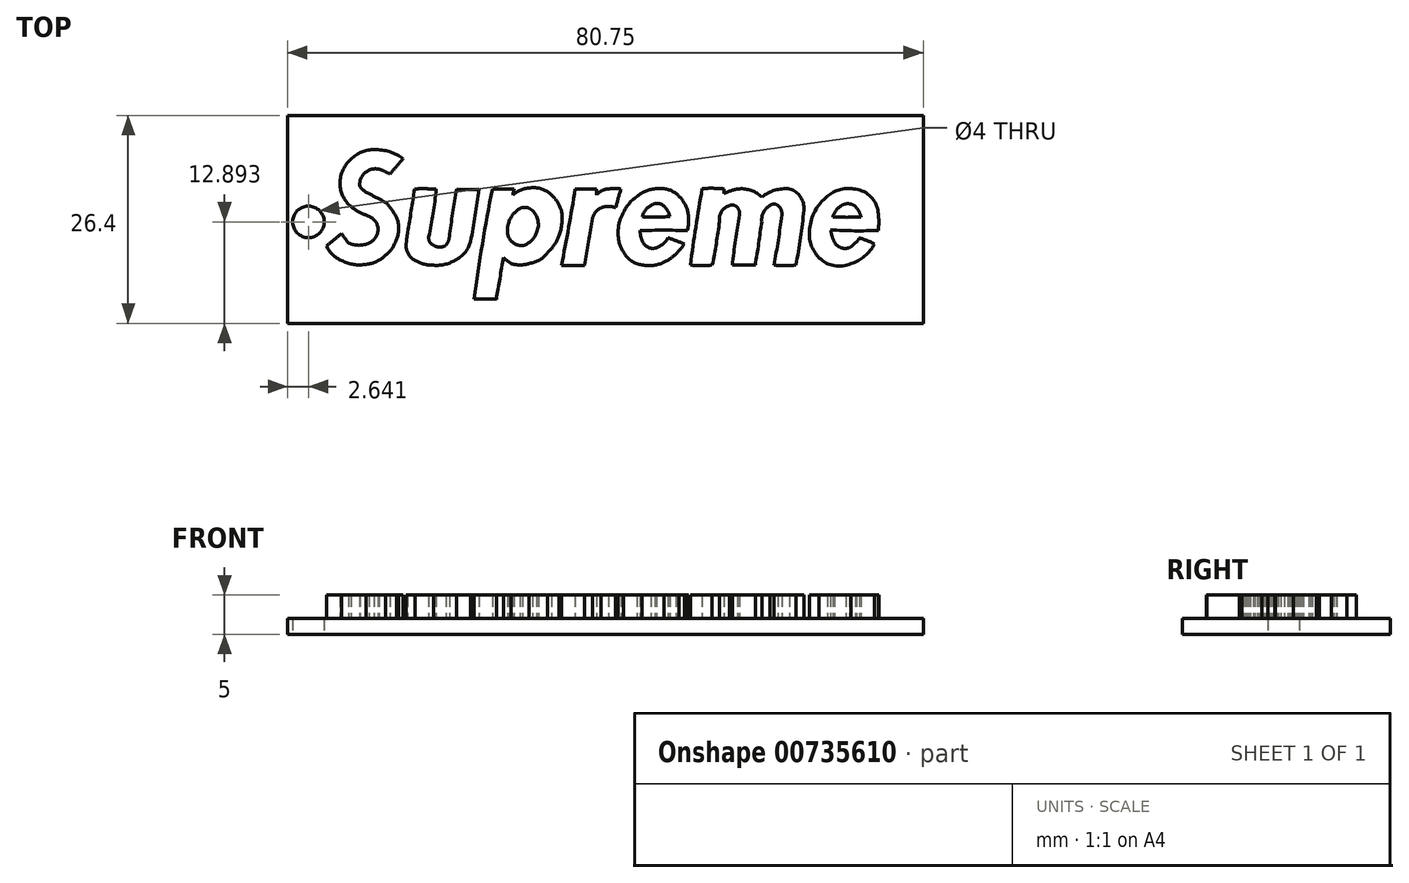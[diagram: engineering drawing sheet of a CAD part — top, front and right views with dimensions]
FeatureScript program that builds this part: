
annotation { "Feature Type Name" : "Feature", "Feature Type Description" : "" }
export const myFeature = defineFeature(function(context is Context, id is Id, definition is map)
    precondition{}
    {
        {
            var Q0;
            Q0=qCreatedBy(makeId("Top.planeOp"),FACE);
            var sketch = newSketch(context, id + "F0", { "sketchPlane" : qUnion([Q0])});
            skArc(sketch, "E0", {"start": v(-34.63, 20.9) * mm, "mid": v(-36.37, 21.8) * mm, "end": v(-38.3, 22.08) * mm});
            skArc(sketch, "E1", {"start": v(-38.3, 22.08) * mm, "mid": v(-39.9, 21.77) * mm, "end": v(-41.25, 20.87) * mm});
            skArc(sketch, "E2", {"start": v(-41.25, 20.87) * mm, "mid": v(-42.35, 19.34) * mm, "end": v(-42.67, 17.5) * mm});
            skArc(sketch, "E3", {"start": v(-42.67, 17.5) * mm, "mid": v(-42.22, 16.03) * mm, "end": v(-41.25, 14.83) * mm});
            skArc(sketch, "E4", {"start": v(-41.25, 14.83) * mm, "mid": v(-40.34, 14.21) * mm, "end": v(-39.34, 13.75) * mm});
            skArc(sketch, "E5", {"start": v(-37.84, 12.2) * mm, "mid": v(-38.36, 13.2) * mm, "end": v(-39.34, 13.75) * mm});
            skArc(sketch, "E6", {"start": v(-38.96, 10.2) * mm, "mid": v(-38.09, 11.03) * mm, "end": v(-37.84, 12.2) * mm});
            skArc(sketch, "E7", {"start": v(-41.55, 10.2) * mm, "mid": v(-40.26, 9.92) * mm, "end": v(-38.96, 10.2) * mm});
            skArc(sketch, "E8", {"start": v(-42.46, 11.41) * mm, "mid": v(-42.03, 10.8) * mm, "end": v(-41.55, 10.2) * mm});
            skArc(sketch, "E9", {"start": v(-44.38, 9.83) * mm, "mid": v(-43.42, 10.62) * mm, "end": v(-42.46, 11.41) * mm});
            skArc(sketch, "E10", {"start": v(-44.38, 9.83) * mm, "mid": v(-43.6, 8.72) * mm, "end": v(-42.46, 8) * mm});
            skArc(sketch, "E11", {"start": v(-42.46, 8) * mm, "mid": v(-40.94, 7.49) * mm, "end": v(-39.34, 7.5) * mm});
            skArc(sketch, "E12", {"start": v(-39.34, 7.5) * mm, "mid": v(-38, 7.88) * mm, "end": v(-36.84, 8.66) * mm});
            skArc(sketch, "E13", {"start": v(-36.84, 8.66) * mm, "mid": v(-36, 9.58) * mm, "end": v(-35.47, 10.7) * mm});
            skArc(sketch, "E14", {"start": v(-35.47, 10.7) * mm, "mid": v(-35.2, 12.08) * mm, "end": v(-35.47, 13.45) * mm});
            skArc(sketch, "E15", {"start": v(-35.47, 13.45) * mm, "mid": v(-36.1, 14.46) * mm, "end": v(-36.84, 15.37) * mm});
            skArc(sketch, "E16", {"start": v(-38.96, 16.5) * mm, "mid": v(-37.91, 15.91) * mm, "end": v(-36.84, 15.37) * mm});
            skArc(sketch, "E17", {"start": v(-40.13, 17.41) * mm, "mid": v(-39.62, 16.85) * mm, "end": v(-38.96, 16.5) * mm});
            skArc(sketch, "E18", {"start": v(-39.34, 19.24) * mm, "mid": v(-40, 18.44) * mm, "end": v(-40.13, 17.41) * mm});
            skArc(sketch, "E19", {"start": v(-37.67, 19.58) * mm, "mid": v(-38.54, 19.6) * mm, "end": v(-39.34, 19.24) * mm});
            skArc(sketch, "E20", {"start": v(-36.3, 18.95) * mm, "mid": v(-36.96, 19.31) * mm, "end": v(-37.67, 19.58) * mm});
            skArc(sketch, "E21", {"start": v(-34.63, 20.9) * mm, "mid": v(-35.48, 19.95) * mm, "end": v(-36.3, 18.95) * mm});
            skArc(sketch, "E22", {"start": v(-30.43, 17.04) * mm, "mid": v(-31.8, 17.1) * mm, "end": v(-33.17, 17.08) * mm});
            skArc(sketch, "E23", {"start": v(-31.38, 10.96) * mm, "mid": v(-30.83, 13.98) * mm, "end": v(-30.43, 17.04) * mm});
            skArc(sketch, "E24", {"start": v(-31.38, 10.96) * mm, "mid": v(-31.25, 10.32) * mm, "end": v(-30.76, 9.91) * mm});
            skArc(sketch, "E25", {"start": v(-30.76, 9.91) * mm, "mid": v(-29.99, 9.7) * mm, "end": v(-29.22, 9.91) * mm});
            skArc(sketch, "E26", {"start": v(-29.22, 9.91) * mm, "mid": v(-28.93, 10.4) * mm, "end": v(-28.76, 10.96) * mm});
            skArc(sketch, "E27", {"start": v(-27.84, 17.04) * mm, "mid": v(-28.35, 14) * mm, "end": v(-28.76, 10.96) * mm});
            skArc(sketch, "E28", {"start": v(-27.84, 17.04) * mm, "mid": v(-26.43, 17.02) * mm, "end": v(-25.02, 17.04) * mm});
            skArc(sketch, "E29", {"start": v(-26.05, 10.42) * mm, "mid": v(-25.5, 13.72) * mm, "end": v(-25.02, 17.04) * mm});
            skArc(sketch, "E30", {"start": v(-27.84, 8.12) * mm, "mid": v(-26.72, 9.1) * mm, "end": v(-26.05, 10.42) * mm});
            skArc(sketch, "E31", {"start": v(-30.76, 7.39) * mm, "mid": v(-29.24, 7.52) * mm, "end": v(-27.84, 8.12) * mm});
            skArc(sketch, "E32", {"start": v(-33.09, 7.97) * mm, "mid": v(-31.97, 7.52) * mm, "end": v(-30.76, 7.39) * mm});
            skArc(sketch, "E33", {"start": v(-34.27, 9.71) * mm, "mid": v(-33.9, 8.7) * mm, "end": v(-33.09, 7.97) * mm});
            skArc(sketch, "E34", {"start": v(-34.06, 11.57) * mm, "mid": v(-34.2, 10.64) * mm, "end": v(-34.27, 9.71) * mm});
            skArc(sketch, "E35", {"start": v(-34.06, 11.57) * mm, "mid": v(-33.61, 14.32) * mm, "end": v(-33.17, 17.08) * mm});
            skArc(sketch, "E36", {"start": v(-20.53, 17.08) * mm, "mid": v(-21.9, 17.08) * mm, "end": v(-23.3, 17.08) * mm});
            skArc(sketch, "E37", {"start": v(-20.53, 17.08) * mm, "mid": v(-20.64, 16.7) * mm, "end": v(-20.68, 16.32) * mm});
            skArc(sketch, "E38", {"start": v(-18.17, 17.23) * mm, "mid": v(-19.5, 17) * mm, "end": v(-20.68, 16.32) * mm});
            skArc(sketch, "E39", {"start": v(-15.79, 16.32) * mm, "mid": v(-16.88, 17.03) * mm, "end": v(-18.17, 17.23) * mm});
            skArc(sketch, "E40", {"start": v(-14.52, 14.32) * mm, "mid": v(-15.03, 15.4) * mm, "end": v(-15.79, 16.32) * mm});
            skArc(sketch, "E41", {"start": v(-14.82, 11.17) * mm, "mid": v(-14.47, 12.73) * mm, "end": v(-14.52, 14.32) * mm});
            skArc(sketch, "E42", {"start": v(-16.27, 9) * mm, "mid": v(-15.41, 10) * mm, "end": v(-14.82, 11.17) * mm});
            skArc(sketch, "E43", {"start": v(-18.62, 7.62) * mm, "mid": v(-17.3, 8.06) * mm, "end": v(-16.27, 9) * mm});
            skArc(sketch, "E44", {"start": v(-20.95, 7.62) * mm, "mid": v(-19.79, 7.42) * mm, "end": v(-18.62, 7.62) * mm});
            skArc(sketch, "E45", {"start": v(-21.9, 8.38) * mm, "mid": v(-21.45, 7.97) * mm, "end": v(-20.95, 7.62) * mm});
            skArc(sketch, "E46", {"start": v(-22.8, 3.08) * mm, "mid": v(-22.35, 5.73) * mm, "end": v(-21.9, 8.38) * mm});
            skArc(sketch, "E47", {"start": v(-22.79, 3.13) * mm, "mid": v(-24.2, 3.11) * mm, "end": v(-25.6, 3.08) * mm});
            skArc(sketch, "E48", {"start": v(-23.3, 17.08) * mm, "mid": v(-24.57, 10.1) * mm, "end": v(-25.6, 3.08) * mm});
            skArc(sketch, "E49", {"start": v(-12.78, 17.08) * mm, "mid": v(-11.42, 17.07) * mm, "end": v(-10.07, 17.08) * mm});
            skArc(sketch, "E50", {"start": v(-10.07, 17.08) * mm, "mid": v(-10.1, 16.7) * mm, "end": v(-10.07, 16.32) * mm});
            skArc(sketch, "E51", {"start": v(-8.53, 17.08) * mm, "mid": v(-9.39, 16.88) * mm, "end": v(-10.07, 16.32) * mm});
            skArc(sketch, "E52", {"start": v(-6.97, 17.08) * mm, "mid": v(-7.75, 17.15) * mm, "end": v(-8.53, 17.08) * mm});
            skArc(sketch, "E53", {"start": v(-6.97, 17.08) * mm, "mid": v(-7.31, 15.9) * mm, "end": v(-7.63, 14.7) * mm});
            skArc(sketch, "E54", {"start": v(-7.63, 14.7) * mm, "mid": v(-8.56, 14.85) * mm, "end": v(-9.48, 14.7) * mm});
            skArc(sketch, "E55", {"start": v(-9.48, 14.7) * mm, "mid": v(-10.17, 14.16) * mm, "end": v(-10.59, 13.39) * mm});
            skArc(sketch, "E56", {"start": v(-11.58, 7.36) * mm, "mid": v(-11.07, 10.37) * mm, "end": v(-10.59, 13.39) * mm});
            skArc(sketch, "E57", {"start": v(-14.52, 7.36) * mm, "mid": v(-13.05, 7.36) * mm, "end": v(-11.58, 7.36) * mm});
            skArc(sketch, "E58", {"start": v(-14.52, 7.36) * mm, "mid": v(-13.61, 12.21) * mm, "end": v(-12.78, 17.08) * mm});
            skArc(sketch, "E59", {"start": v(-4.25, 13.54) * mm, "mid": v(-2.5, 13.5) * mm, "end": v(-0.77, 13.58) * mm});
            skArc(sketch, "E60", {"start": v(-3.15, 14.96) * mm, "mid": v(-3.87, 14.39) * mm, "end": v(-4.25, 13.54) * mm});
            skArc(sketch, "E61", {"start": v(-1.6, 14.96) * mm, "mid": v(-2.38, 15.23) * mm, "end": v(-3.15, 14.96) * mm});
            skArc(sketch, "E62", {"start": v(-0.77, 13.58) * mm, "mid": v(-1.06, 14.35) * mm, "end": v(-1.6, 14.96) * mm});
            skArc(sketch, "E63", {"start": v(-2.67, 9.55) * mm, "mid": v(-1.7, 10.04) * mm, "end": v(-0.98, 10.88) * mm});
            skArc(sketch, "E64", {"start": v(-4.29, 10.53) * mm, "mid": v(-3.66, 9.74) * mm, "end": v(-2.67, 9.55) * mm});
            skArc(sketch, "E65", {"start": v(-4.55, 11.8) * mm, "mid": v(-4.47, 11.15) * mm, "end": v(-4.29, 10.53) * mm});
            skArc(sketch, "E66", {"start": v(1.48, 11.8) * mm, "mid": v(-1.54, 11.83) * mm, "end": v(-4.55, 11.8) * mm});
            skArc(sketch, "E67", {"start": v(1.48, 11.8) * mm, "mid": v(1.62, 13.1) * mm, "end": v(1.48, 14.4) * mm});
            skArc(sketch, "E68", {"start": v(1.48, 14.4) * mm, "mid": v(0.9, 15.57) * mm, "end": v(0, 16.52) * mm});
            skArc(sketch, "E69", {"start": v(0, 16.52) * mm, "mid": v(-1.16, 17.06) * mm, "end": v(-2.43, 17.12) * mm});
            skArc(sketch, "E70", {"start": v(-2.43, 17.12) * mm, "mid": v(-3.78, 16.83) * mm, "end": v(-4.95, 16.1) * mm});
            skArc(sketch, "E71", {"start": v(-4.95, 16.1) * mm, "mid": v(-6.03, 15.11) * mm, "end": v(-6.76, 13.84) * mm});
            skArc(sketch, "E72", {"start": v(-6.76, 13.84) * mm, "mid": v(-7.19, 12.77) * mm, "end": v(-7.32, 11.62) * mm});
            skArc(sketch, "E73", {"start": v(-7.32, 11.62) * mm, "mid": v(-7.19, 10.27) * mm, "end": v(-6.63, 9.04) * mm});
            skArc(sketch, "E74", {"start": v(-6.63, 9.04) * mm, "mid": v(-5.65, 7.94) * mm, "end": v(-4.27, 7.43) * mm});
            skArc(sketch, "E75", {"start": v(-4.27, 7.43) * mm, "mid": v(-2.85, 7.36) * mm, "end": v(-1.48, 7.78) * mm});
            skArc(sketch, "E76", {"start": v(-1.48, 7.78) * mm, "mid": v(-0.46, 8.4) * mm, "end": v(0.4, 9.24) * mm});
            skArc(sketch, "E77", {"start": v(0.4, 9.24) * mm, "mid": v(0.76, 9.65) * mm, "end": v(1.07, 10.11) * mm});
            skArc(sketch, "E78", {"start": v(1.07, 10.11) * mm, "mid": v(0.05, 10.5) * mm, "end": v(-0.98, 10.88) * mm});
            skArc(sketch, "E79", {"start": v(6.1, 17.1) * mm, "mid": v(4.72, 17.16) * mm, "end": v(3.34, 17.13) * mm});
            skArc(sketch, "E80", {"start": v(3.34, 17.13) * mm, "mid": v(2.55, 12.27) * mm, "end": v(1.85, 7.4) * mm});
            skArc(sketch, "E81", {"start": v(1.85, 7.4) * mm, "mid": v(3.24, 7.35) * mm, "end": v(4.62, 7.4) * mm});
            skArc(sketch, "E82", {"start": v(4.62, 7.4) * mm, "mid": v(5.14, 10.16) * mm, "end": v(5.55, 12.94) * mm});
            skArc(sketch, "E83", {"start": v(6.83, 14.98) * mm, "mid": v(5.8, 14.2) * mm, "end": v(5.55, 12.94) * mm});
            skArc(sketch, "E84", {"start": v(7.86, 14.69) * mm, "mid": v(7.4, 15.02) * mm, "end": v(6.83, 14.98) * mm});
            skArc(sketch, "E85", {"start": v(8.1, 13.76) * mm, "mid": v(8.07, 14.25) * mm, "end": v(7.86, 14.69) * mm});
            skArc(sketch, "E86", {"start": v(8.1, 13.76) * mm, "mid": v(7.57, 10.59) * mm, "end": v(7.19, 7.4) * mm});
            skArc(sketch, "E87", {"start": v(10.1, 7.4) * mm, "mid": v(8.64, 7.4) * mm, "end": v(7.19, 7.4) * mm});
            skArc(sketch, "E88", {"start": v(10.1, 7.4) * mm, "mid": v(10.52, 10.17) * mm, "end": v(10.91, 12.94) * mm});
            skArc(sketch, "E89", {"start": v(11.93, 14.98) * mm, "mid": v(11.13, 14.1) * mm, "end": v(10.91, 12.94) * mm});
            skArc(sketch, "E90", {"start": v(13, 14.98) * mm, "mid": v(12.46, 15.16) * mm, "end": v(11.93, 14.98) * mm});
            skArc(sketch, "E91", {"start": v(13.47, 13.76) * mm, "mid": v(13.38, 14.43) * mm, "end": v(13, 14.98) * mm});
            skArc(sketch, "E92", {"start": v(12.46, 7.4) * mm, "mid": v(13.02, 10.57) * mm, "end": v(13.47, 13.76) * mm});
            skPoint(sketch, "E92.startSnap0", {"position": v(12.46, 15.16) * mm});
            skArc(sketch, "E93", {"start": v(12.46, 7.4) * mm, "mid": v(13.86, 7.32) * mm, "end": v(15.25, 7.4) * mm});
            skArc(sketch, "E94", {"start": v(15.25, 7.4) * mm, "mid": v(15.86, 10.89) * mm, "end": v(16.27, 14.4) * mm});
            skArc(sketch, "E95", {"start": v(16.27, 14.4) * mm, "mid": v(15.84, 16.06) * mm, "end": v(14.47, 17.1) * mm});
            skArc(sketch, "E96", {"start": v(14.47, 17.1) * mm, "mid": v(12.6, 16.91) * mm, "end": v(10.91, 16.06) * mm});
            skPoint(sketch, "E96.endSnap0", {"position": v(15.84, 16.06) * mm});
            skArc(sketch, "E97", {"start": v(10.91, 16.06) * mm, "mid": v(9.61, 16.87) * mm, "end": v(8.1, 17.1) * mm});
            skArc(sketch, "E98", {"start": v(8.1, 17.1) * mm, "mid": v(7.07, 16.88) * mm, "end": v(6.1, 16.47) * mm});
            skArc(sketch, "E99", {"start": v(6.1, 16.47) * mm, "mid": v(6.11, 16.78) * mm, "end": v(6.1, 17.1) * mm});
            skArc(sketch, "E100", {"start": v(19.67, 11.88) * mm, "mid": v(22.7, 11.76) * mm, "end": v(25.72, 11.83) * mm});
            skArc(sketch, "E101", {"start": v(19.67, 11.88) * mm, "mid": v(19.85, 11.06) * mm, "end": v(20.17, 10.27) * mm});
            skArc(sketch, "E102", {"start": v(20.17, 10.27) * mm, "mid": v(20.78, 9.69) * mm, "end": v(21.6, 9.52) * mm});
            skArc(sketch, "E103", {"start": v(21.6, 9.52) * mm, "mid": v(22.3, 9.76) * mm, "end": v(22.84, 10.27) * mm});
            skArc(sketch, "E104", {"start": v(22.84, 10.27) * mm, "mid": v(23.13, 10.53) * mm, "end": v(23.3, 10.87) * mm});
            skArc(sketch, "E105", {"start": v(25.23, 10.1) * mm, "mid": v(24.28, 10.52) * mm, "end": v(23.3, 10.87) * mm});
            skArc(sketch, "E106", {"start": v(22.25, 7.59) * mm, "mid": v(24, 8.54) * mm, "end": v(25.23, 10.1) * mm});
            skArc(sketch, "E107", {"start": v(18.21, 8.33) * mm, "mid": v(20.11, 7.33) * mm, "end": v(22.25, 7.59) * mm});
            skArc(sketch, "E108", {"start": v(17, 11.97) * mm, "mid": v(17.17, 10) * mm, "end": v(18.21, 8.33) * mm});
            skArc(sketch, "E109", {"start": v(19.26, 16.15) * mm, "mid": v(17.69, 14.3) * mm, "end": v(17, 11.97) * mm});
            skArc(sketch, "E110", {"start": v(22.84, 17.05) * mm, "mid": v(20.94, 17.02) * mm, "end": v(19.26, 16.15) * mm});
            skArc(sketch, "E111", {"start": v(25.7, 14.1) * mm, "mid": v(24.79, 16.08) * mm, "end": v(22.84, 17.05) * mm});
            skArc(sketch, "E112", {"start": v(25.72, 11.83) * mm, "mid": v(25.78, 12.97) * mm, "end": v(25.7, 14.1) * mm});
            skArc(sketch, "E113", {"start": v(20.96, 14.93) * mm, "mid": v(20.33, 14.32) * mm, "end": v(19.96, 13.54) * mm});
            skArc(sketch, "E114", {"start": v(22.06, 15.19) * mm, "mid": v(21.48, 15.16) * mm, "end": v(20.96, 14.93) * mm});
            skArc(sketch, "E115", {"start": v(22.98, 14.62) * mm, "mid": v(22.6, 15.02) * mm, "end": v(22.06, 15.19) * mm});
            skArc(sketch, "E116", {"start": v(23.5, 13.54) * mm, "mid": v(23.31, 14.11) * mm, "end": v(22.98, 14.62) * mm});
            skArc(sketch, "E117", {"start": v(19.96, 13.54) * mm, "mid": v(21.73, 13.48) * mm, "end": v(23.5, 13.54) * mm});
            skArc(sketch, "E118", {"start": v(-17.71, 11.54) * mm, "mid": v(-17.55, 13.25) * mm, "end": v(-18.59, 14.62) * mm});
            skArc(sketch, "E119", {"start": v(-19.48, 9.86) * mm, "mid": v(-18.37, 10.47) * mm, "end": v(-17.71, 11.54) * mm});
            skArc(sketch, "E120", {"start": v(-21, 10.52) * mm, "mid": v(-20.3, 10.03) * mm, "end": v(-19.48, 9.86) * mm});
            skArc(sketch, "E121", {"start": v(-21.3, 12.53) * mm, "mid": v(-21.38, 11.5) * mm, "end": v(-21, 10.52) * mm});
            skArc(sketch, "E122", {"start": v(-19.79, 14.62) * mm, "mid": v(-20.76, 13.74) * mm, "end": v(-21.3, 12.53) * mm});
            skArc(sketch, "E123", {"start": v(-18.59, 14.62) * mm, "mid": v(-19.19, 14.74) * mm, "end": v(-19.79, 14.62) * mm});
            skSolve(sketch);
        }
        {
            var Q0;
            Q0=qCreatedBy(makeId("Top.planeOp"),FACE);
            var sketch = newSketch(context, id + "F1", { "sketchPlane" : qUnion([Q0])});
            skLineSegment(sketch, "E124.bottom", {"start": v(-49.31, 0) * mm, "end": v(31.44, 0) * mm});
            skLineSegment(sketch, "E124.top", {"start": v(-49.31, 26.4) * mm, "end": v(31.44, 26.4) * mm});
            skLineSegment(sketch, "E124.left", {"start": v(-49.31, 0) * mm, "end": v(-49.31, 26.4) * mm});
            skLineSegment(sketch, "E124.right", {"start": v(31.44, 0) * mm, "end": v(31.44, 26.4) * mm});
            skPoint(sketch, "E124.middle", {"position": v(-8.93, 13.2) * mm});
            skCircle(sketch, "E125", {"center": v(-46.67, 12.9) * mm, "radius": 2 * mm});
            skSolve(sketch);
        }
        {
            var Q0;
            Q0=makeQuery(id+"F1.imprint","IMPRINT",FACE,{"disambiguationData":[TD([[makeQuery(id+"F1.imprint","IMPRINT",EDGE,{"derivedFrom":sQuery(id+"F1.wireOp",EDGE,"E124.bottom")}),1.0]])]});
            extrude(context, id + "F2", {"entities" : qUnion([Q0]), "flatOperationType" : FlatOperationType.REMOVE, "depth" : 2 * mm, "offsetDistance" : 25 * mm, "domain" : OperationDomain.MODEL});
        }
        {
            var Q0;
            Q0=makeQuery(id+"F0.imprint","IMPRINT",FACE,{"disambiguationData":[TD([[makeQuery(id+"F0.imprint","IMPRINT",EDGE,{"derivedFrom":sQuery(id+"F0.wireOp",EDGE,"E0")}),1.0]])]});
            var Q1;
            Q1=makeQuery(id+"F0.imprint","IMPRINT",FACE,{"disambiguationData":[TD([[makeQuery(id+"F0.imprint","IMPRINT",EDGE,{"derivedFrom":sQuery(id+"F0.wireOp",EDGE,"E22")}),1.0]])]});
            var Q2;
            Q2=makeQuery(id+"F0.imprint","IMPRINT",FACE,{"disambiguationData":[TD([[makeQuery(id+"F0.imprint","IMPRINT",EDGE,{"derivedFrom":sQuery(id+"F0.wireOp",EDGE,"E36")}),1.0]])]});
            var Q3;
            Q3=makeQuery(id+"F0.imprint","IMPRINT",FACE,{"disambiguationData":[TD([[makeQuery(id+"F0.imprint","IMPRINT",EDGE,{"derivedFrom":sQuery(id+"F0.wireOp",EDGE,"E49")}),-1.0]])]});
            var Q4;
            Q4=makeQuery(id+"F0.imprint","IMPRINT",FACE,{"disambiguationData":[TD([[makeQuery(id+"F0.imprint","IMPRINT",EDGE,{"derivedFrom":sQuery(id+"F0.wireOp",EDGE,"E59")}),-1.0]])]});
            var Q5;
            Q5=makeQuery(id+"F0.imprint","IMPRINT",FACE,{"disambiguationData":[TD([[makeQuery(id+"F0.imprint","IMPRINT",EDGE,{"derivedFrom":sQuery(id+"F0.wireOp",EDGE,"E79")}),1.0]])]});
            var Q6;
            Q6=makeQuery(id+"F0.imprint","IMPRINT",FACE,{"disambiguationData":[TD([[makeQuery(id+"F0.imprint","IMPRINT",EDGE,{"derivedFrom":sQuery(id+"F0.wireOp",EDGE,"E100")}),1.0]])]});
            extrude(context, id + "F3", {"entities" : qUnion([Q0, Q1, Q2, Q3, Q4, Q5, Q6]), "operationType" : NewBodyOperationType.ADD, "flatOperationType" : FlatOperationType.REMOVE, "depth" : 5 * mm, "offsetDistance" : 25 * mm, "domain" : OperationDomain.MODEL});
        }
    });
